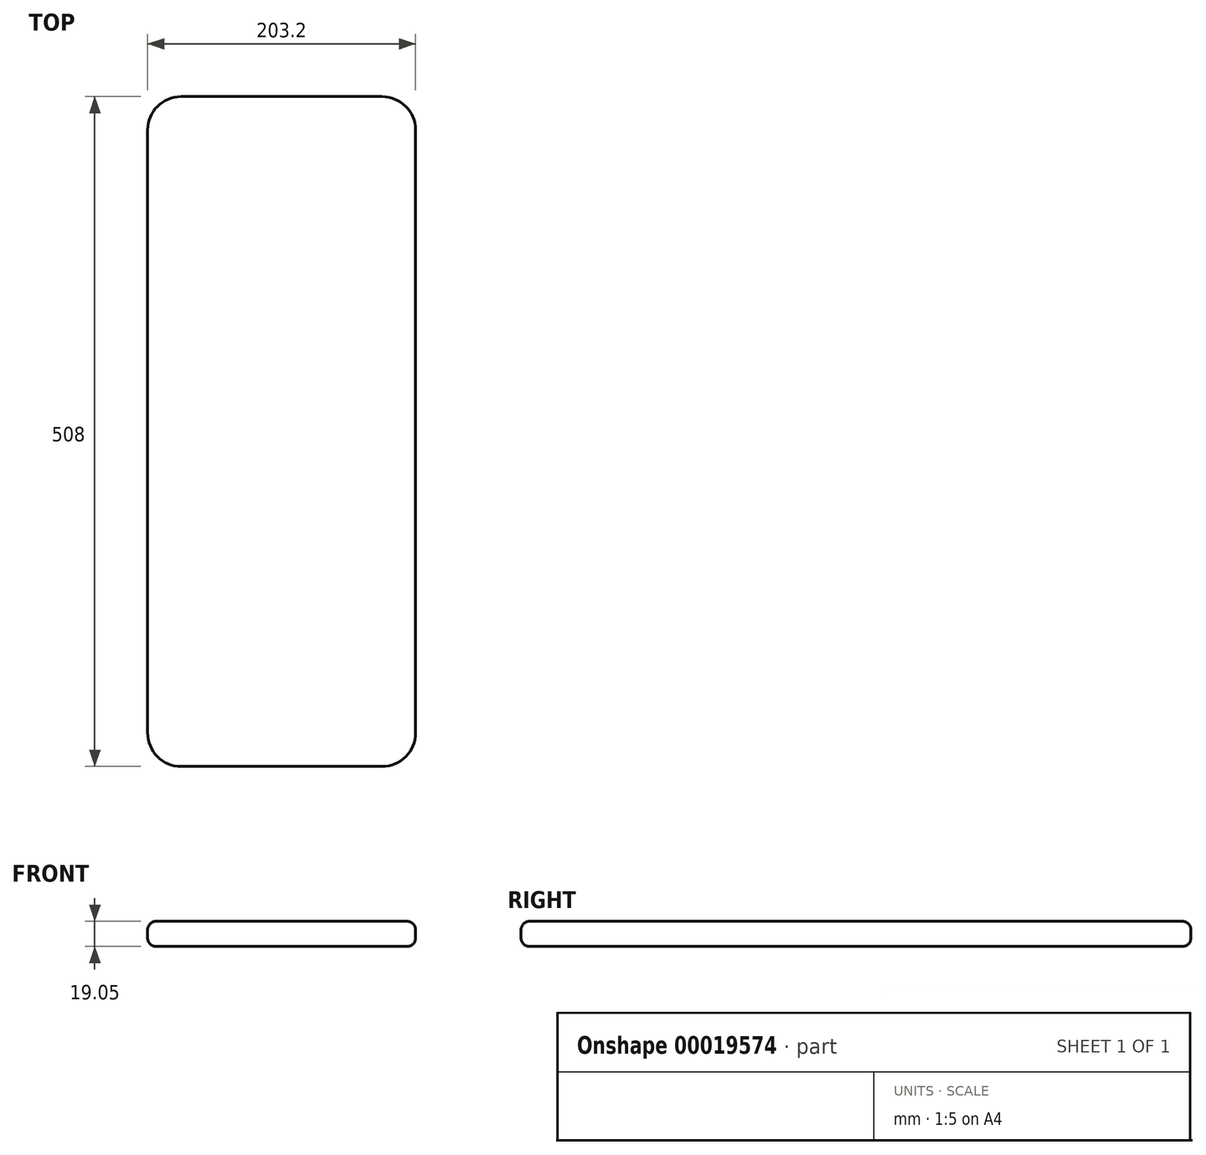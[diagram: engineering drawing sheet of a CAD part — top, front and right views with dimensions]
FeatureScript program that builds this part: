
annotation { "Feature Type Name" : "Feature", "Feature Type Description" : "" }
export const myFeature = defineFeature(function(context is Context, id is Id, definition is map)
    precondition{}
    {
        {
            var Q0;
            Q0=qCreatedBy(makeId("Front.planeOp"),FACE);
            var sketch = newSketch(context, id + "F0", { "sketchPlane" : qUnion([Q0])});
            skLineSegment(sketch, "E0.bottom", {"start": v(0, 0) * mm, "end": v(203.2, 0) * mm});
            skLineSegment(sketch, "E0.top", {"start": v(0, 19.05) * mm, "end": v(203.2, 19.05) * mm});
            skLineSegment(sketch, "E0.left", {"start": v(0, 0) * mm, "end": v(0, 19.05) * mm});
            skLineSegment(sketch, "E0.right", {"start": v(203.2, 0) * mm, "end": v(203.2, 19.05) * mm});
            skSolve(sketch);
        }
        {
            var Q0;
            Q0=makeQuery(id+"F0.imprint","IMPRINT",FACE,{"disambiguationData":[TD([[makeQuery(id+"F0.imprint","IMPRINT",EDGE,{"derivedFrom":sQuery(id+"F0.wireOp",EDGE,"E0.bottom")}),1.0]])]});
            extrude(context, id + "F1", {"entities" : qUnion([Q0]), "depth" : 508 * mm});
        }
        {
            var Q0;
            Q0=makeQuery(id+"F1.opExtrude","CAP_EDGE",EDGE,{"disambiguationData":[OSD([sQuery(id+"F0.wireOp",EDGE,"E0.right")])],"isStart":false});
            var Q1;
            Q1=makeQuery(id+"F1.opExtrude","CAP_EDGE",EDGE,{"disambiguationData":[OSD([sQuery(id+"F0.wireOp",EDGE,"E0.left")])],"isStart":false});
            var Q2;
            Q2=makeQuery(id+"F1.opExtrude","CAP_EDGE",EDGE,{"disambiguationData":[OSD([sQuery(id+"F0.wireOp",EDGE,"E0.right")])],"isStart":true});
            var Q3;
            Q3=makeQuery(id+"F1.opExtrude","CAP_EDGE",EDGE,{"disambiguationData":[OSD([sQuery(id+"F0.wireOp",EDGE,"E0.left")])],"isStart":true});
            fillet(context, id + "F2", {"entities" : qUnion([Q0, Q1, Q2, Q3]), "radius" : 25.4 * mm, "tangentPropagation" : true, "allowEdgeOverflow" : false});
        }
        {
            var Q0;
            Q0=makeQuery(id+"F1.opExtrude","SWEPT_FACE",FACE,{"disambiguationData":[OSD([sQuery(id+"F0.wireOp",EDGE,"E0.top")])]});
            var Q1;
            Q1=makeQuery(id+"F1.opExtrude","SWEPT_FACE",FACE,{"disambiguationData":[OSD([sQuery(id+"F0.wireOp",EDGE,"E0.bottom")])]});
            fillet(context, id + "F3", {"entities" : qUnion([Q0, Q1]), "radius" : 6.35 * mm, "tangentPropagation" : true, "allowEdgeOverflow" : false});
        }
    });
